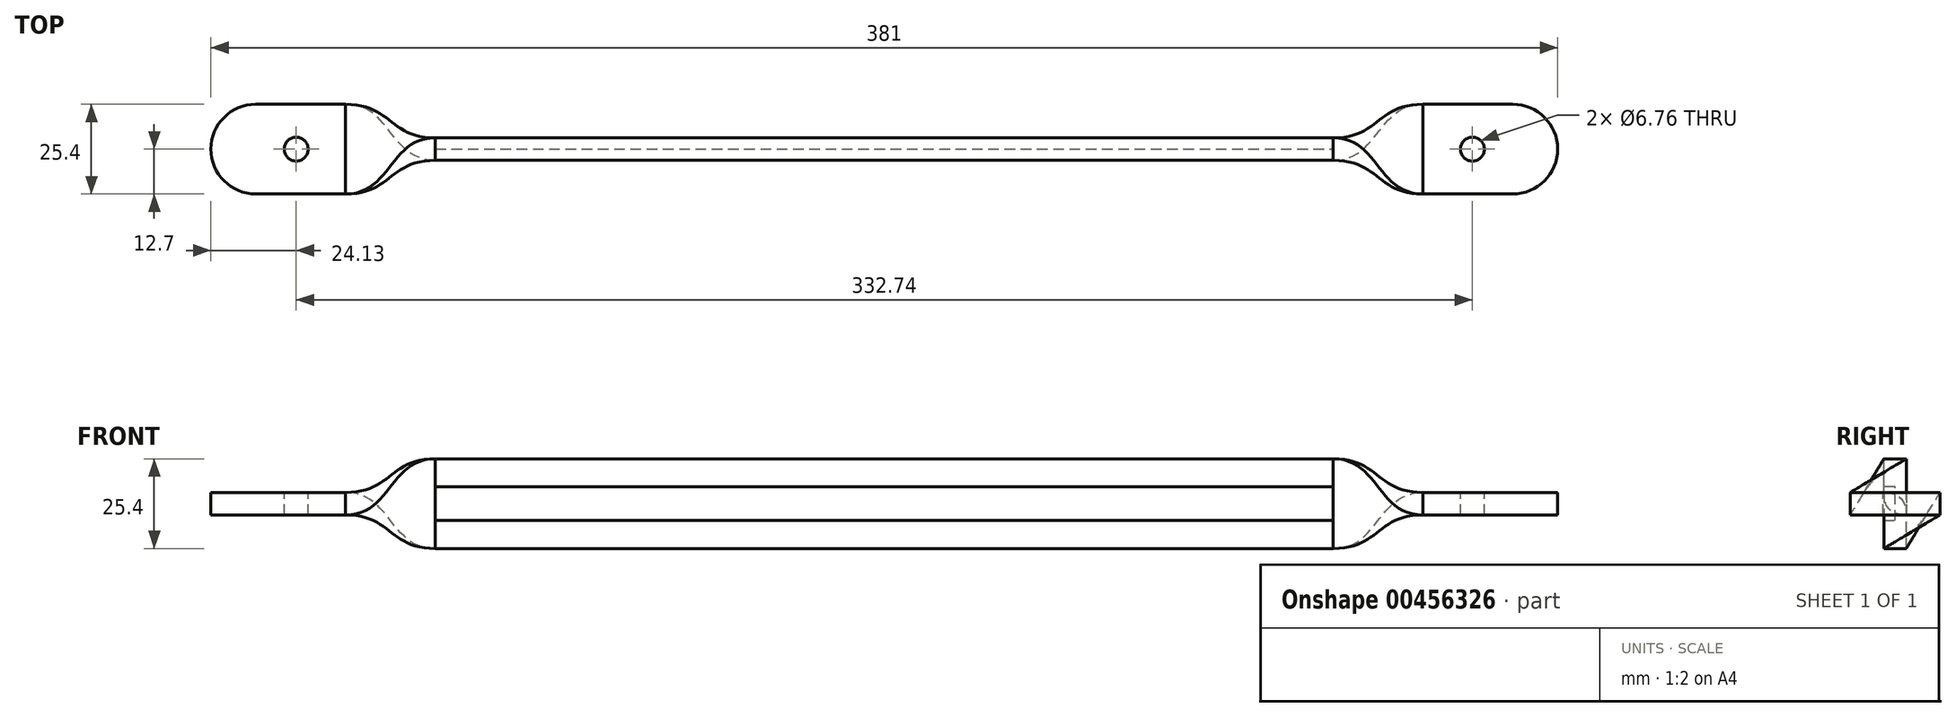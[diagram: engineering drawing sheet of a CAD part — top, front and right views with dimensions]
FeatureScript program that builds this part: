
annotation { "Feature Type Name" : "Feature", "Feature Type Description" : "" }
export const myFeature = defineFeature(function(context is Context, id is Id, definition is map)
    precondition{}
    {
        {
            var Q0;
            Q0=qCreatedBy(makeId("Top.planeOp"),FACE);
            var sketch = newSketch(context, id + "F0", { "sketchPlane" : qUnion([Q0])});
            skPoint(sketch, "E0", {"position": v(-152.4, 12.7) * mm});
            skPoint(sketch, "E1", {"position": v(-152.4, -12.7) * mm});
            skPoint(sketch, "E2", {"position": v(0, 0) * mm});
            skPoint(sketch, "E3", {"position": v(-190.5, 12.7) * mm});
            skPoint(sketch, "E4", {"position": v(-190.5, -12.7) * mm});
            skLineSegment(sketch, "E5", {"start": v(-190.5, 0) * mm, "end": v(190.5, 0) * mm, "construction": true});
            skLineSegment(sketch, "E6", {"start": v(-177.8, 12.7) * mm, "end": v(-152.4, 12.7) * mm});
            skLineSegment(sketch, "E7", {"start": v(-152.4, -12.7) * mm, "end": v(-152.4, 12.7) * mm});
            skLineSegment(sketch, "E8", {"start": v(-177.8, -12.7) * mm, "end": v(-152.4, -12.7) * mm});
            skLineSegment(sketch, "E9", {"start": v(-190.5, 0) * mm, "end": v(-190.5, 0) * mm});
            skLineSegment(sketch, "E10", {"start": v(0, 12.7) * mm, "end": v(0, -12.7) * mm, "construction": true});
            skPoint(sketch, "E11", {"position": v(-166.37, 0) * mm});
            skArc(sketch, "E12.filletArc", {"start": v(-190.5, 0) * mm, "mid": v(-186.78, -8.98) * mm, "end": v(-177.8, -12.7) * mm});
            skArc(sketch, "E13.filletArc", {"start": v(-177.8, 12.7) * mm, "mid": v(-186.78, 8.98) * mm, "end": v(-190.5, 0) * mm});
            skSolve(sketch);
        }
        {
            var Q0;
            Q0=makeQuery(id+"F0.imprint","IMPRINT",FACE,{"disambiguationData":[TD([[makeQuery(id+"F0.imprint","IMPRINT",EDGE,{"derivedFrom":sQuery(id+"F0.wireOp",EDGE,"33ddd2f7-314b-40ee-8d08-8bc8de4d81912.MirrorCS")}),1.0]])]});
            var Q1;
            Q1=makeQuery(id+"F0.imprint","IMPRINT",FACE,{"disambiguationData":[TD([[makeQuery(id+"F0.imprint","IMPRINT",EDGE,{"derivedFrom":sQuery(id+"F0.wireOp",EDGE,"E6")}),-1.0]])]});
            extrude(context, id + "F1", {"entities" : qUnion([Q0, Q1]), "endBound" : BoundingType.SYMMETRIC, "depth" : 6.35 * mm});
        }
        {
            var Q0;
            Q0=sQuery(id+"F0.wireOp",VERTEX,"E11");
            var Q1;
            Q1=makeQuery(id+"F1.opExtrude","SWEPT_BODY",BODY,{"disambiguationData":[OSD([sQuery(id+"F0.wireOp",EDGE,"E6"),sQuery(id+"F0.wireOp",EDGE,"E7"),sQuery(id+"F0.wireOp",EDGE,"E8"),sQuery(id+"F0.wireOp",EDGE,"E12.filletArc"),sQuery(id+"F0.wireOp",EDGE,"E13.filletArc")])]});
            hole(context, id + "F2", {"style" : HoleStyle.SIMPLE, "endStyle" : HoleEndStyle.THROUGH, "standardTappedOrClearance" : lookupTablePath({ "standard" : "ANSI", "fit" : "Normal (ASME)", "size" : "1/4", "type" : "Clearance" }), "standardBlindInLast" : lookupTablePath({ "fit" : "Free", "standard" : "ANSI", "size" : "1/4", "type" : "Clearance" }), "holeDiameter" : 6.76 * mm, "isTappedThrough" : true, "tappedDepth" : 12.7 * mm, "tapClearance" : 3, "locations" : qUnion([Q0]), "scope" : qUnion([Q1])});
        }
        {
            var Q0;
            Q0=sQuery(id+"F0.wireOp",VERTEX,"E11");
            var Q1;
            Q1=makeQuery(id+"F1.opExtrude","SWEPT_BODY",BODY,{"disambiguationData":[OSD([sQuery(id+"F0.wireOp",EDGE,"E6"),sQuery(id+"F0.wireOp",EDGE,"E7"),sQuery(id+"F0.wireOp",EDGE,"E8"),sQuery(id+"F0.wireOp",EDGE,"E12.filletArc"),sQuery(id+"F0.wireOp",EDGE,"E13.filletArc")])]});
            hole(context, id + "F3", {"style" : HoleStyle.SIMPLE, "endStyle" : HoleEndStyle.THROUGH, "oppositeDirection" : true, "standardTappedOrClearance" : lookupTablePath({ "standard" : "ANSI", "fit" : "Normal (ASME)", "size" : "1/4", "type" : "Clearance" }), "standardBlindInLast" : lookupTablePath({ "fit" : "Free", "standard" : "ANSI", "size" : "1/4", "type" : "Clearance" }), "holeDiameter" : 6.76 * mm, "isTappedThrough" : true, "tappedDepth" : 12.7 * mm, "tapClearance" : 3, "locations" : qUnion([Q0]), "scope" : qUnion([Q1])});
        }
        {
            var Q0;
            Q0=makeQuery(id+"F1.opExtrude","SWEPT_BODY",BODY,{"disambiguationData":[OSD([sQuery(id+"F0.wireOp",EDGE,"E6"),sQuery(id+"F0.wireOp",EDGE,"E7"),sQuery(id+"F0.wireOp",EDGE,"E8"),sQuery(id+"F0.wireOp",EDGE,"E12.filletArc"),sQuery(id+"F0.wireOp",EDGE,"E13.filletArc")])]});
            var Q1;
            Q1=qCreatedBy(makeId("Right.planeOp"),FACE);
            mirror(context, id + "F4", {"entities" : qUnion([Q0]), "mirrorPlane" : qUnion([Q1])});
        }
        {
            var Q0;
            Q0=qCreatedBy(makeId("Front.planeOp"),FACE);
            var sketch = newSketch(context, id + "F5", { "sketchPlane" : qUnion([Q0])});
            skPoint(sketch, "E14", {"position": v(0, 0) * mm});
            skLineSegment(sketch, "E15", {"start": v(-127, 0) * mm, "end": v(127, 0) * mm, "construction": true});
            skLineSegment(sketch, "E16", {"start": v(0, -12.7) * mm, "end": v(0, 12.7) * mm, "construction": true});
            skPoint(sketch, "E17", {"position": v(-127, -12.7) * mm});
            skPoint(sketch, "E18", {"position": v(-127, 12.7) * mm});
            skPoint(sketch, "E19", {"position": v(127, -12.7) * mm});
            skPoint(sketch, "E20", {"position": v(127, 12.7) * mm});
            skLineSegment(sketch, "E21", {"start": v(-127, -12.7) * mm, "end": v(-127, 12.7) * mm});
            skLineSegment(sketch, "E22", {"start": v(-127, 12.7) * mm, "end": v(127, 12.7) * mm});
            skLineSegment(sketch, "E23", {"start": v(127, 12.7) * mm, "end": v(127, -12.7) * mm});
            skLineSegment(sketch, "E24", {"start": v(127, -12.7) * mm, "end": v(-127, -12.7) * mm});
            skSolve(sketch);
        }
        {
            var Q0;
            Q0=makeQuery(id+"F5.imprint","IMPRINT",FACE,{"disambiguationData":[TD([[makeQuery(id+"F5.imprint","IMPRINT",EDGE,{"derivedFrom":sQuery(id+"F5.wireOp",EDGE,"E21")}),-1.0]])]});
            extrude(context, id + "F6", {"entities" : qUnion([Q0]), "endBound" : BoundingType.SYMMETRIC, "oppositeDirection" : true, "depth" : 6.35 * mm});
        }
        {
            var Q0;
            Q0=makeQuery(id+"F6.opExtrude","SWEPT_FACE",FACE,{"disambiguationData":[OSD([sQuery(id+"F5.wireOp",EDGE,"E21")])]});
            var Q1;
            Q1=makeQuery(id+"F1.opExtrude","SWEPT_FACE",FACE,{"disambiguationData":[OSD([sQuery(id+"F0.wireOp",EDGE,"E7")])]});
            var Q2;
            Q2=makeQuery(id+"F1.opExtrude","CAP_VERTEX",VERTEX,{"disambiguationData":[OSD([sQuery(id+"F0.wireOp",EDGE,"E6"),sQuery(id+"F0.wireOp",EDGE,"E7")])],"isStart":false});
            var Q3;
            Q3=makeQuery(id+"F6.opExtrude","CAP_VERTEX",VERTEX,{"disambiguationData":[OSD([sQuery(id+"F5.wireOp",EDGE,"E21"),sQuery(id+"F5.wireOp",EDGE,"E24")])],"isStart":false});
            loft(context, id + "F7", {"startCondition" : LoftEndDerivativeType.NORMAL_TO_PROFILE, "startMagnitude" : 1.5, "endCondition" : LoftEndDerivativeType.NORMAL_TO_PROFILE, "endMagnitude" : 1.5, "sheetProfilesArray" : [{ "sheetProfileEntities" : qUnion([Q0]) }, { "sheetProfileEntities" : qUnion([Q1]) }], "matchConnections" : true, "connections" : [{ "connectionEntities" : qUnion([Q2, Q3]), "connectionEdgeQueries" : qUnion([]), "connectionEdgeParameters" : [] }]});
        }
        {
            var Q0;
            Q0=makeQuery(id+"F6.opExtrude","SWEPT_FACE",FACE,{"disambiguationData":[OSD([sQuery(id+"F5.wireOp",EDGE,"E23")])]});
            var Q1;
            Q1=makeQuery(id+"F4.opPattern","COPY",FACE,{"derivedFrom":makeQuery(id+"F1.opExtrude","SWEPT_FACE",FACE,{"disambiguationData":[OSD([sQuery(id+"F0.wireOp",EDGE,"E7")])]}),"instanceName":"1"});
            var Q2;
            Q2=makeQuery(id+"F4.opPattern","COPY",VERTEX,{"derivedFrom":makeQuery(id+"F1.opExtrude","CAP_VERTEX",VERTEX,{"disambiguationData":[OSD([sQuery(id+"F0.wireOp",EDGE,"E6"),sQuery(id+"F0.wireOp",EDGE,"E7")])],"isStart":false}),"instanceName":"1"});
            var Q3;
            Q3=makeQuery(id+"F6.opExtrude","CAP_VERTEX",VERTEX,{"disambiguationData":[OSD([sQuery(id+"F5.wireOp",EDGE,"E23"),sQuery(id+"F5.wireOp",EDGE,"E24")])],"isStart":false});
            loft(context, id + "F8", {"startCondition" : LoftEndDerivativeType.NORMAL_TO_PROFILE, "startMagnitude" : 1.5, "endCondition" : LoftEndDerivativeType.NORMAL_TO_PROFILE, "endMagnitude" : 1.5, "sheetProfilesArray" : [{ "sheetProfileEntities" : qUnion([Q0]) }, { "sheetProfileEntities" : qUnion([Q1]) }], "matchConnections" : true, "connections" : [{ "connectionEntities" : qUnion([Q2, Q3]), "connectionEdgeQueries" : qUnion([]), "connectionEdgeParameters" : [] }]});
        }
        {
            var Q0;
            Q0=qCreatedBy(makeId("Right.planeOp"),FACE);
            var sketch = newSketch(context, id + "F9", { "sketchPlane" : qUnion([Q0])});
            skPoint(sketch, "E25", {"position": v(0, 0) * mm});
            skLineSegment(sketch, "E26", {"start": v(0, 4.76) * mm, "end": v(0, -4.76) * mm});
            skPoint(sketch, "E27", {"position": v(-3.18, -4.76) * mm});
            skPoint(sketch, "E28", {"position": v(-3.18, 4.76) * mm});
            skLineSegment(sketch, "E29", {"start": v(0, -4.76) * mm, "end": v(-3.18, -4.76) * mm});
            skLineSegment(sketch, "E30", {"start": v(-3.18, 4.76) * mm, "end": v(-3.18, -4.76) * mm});
            skLineSegment(sketch, "E31", {"start": v(-3.18, 4.76) * mm, "end": v(0, 4.76) * mm});
            skSolve(sketch);
        }
        {
            var Q0;
            Q0=qSketchRegion(id+"F9",true);
            var Q1;
            Q1=makeQuery(id+"F6.opExtrude","SWEPT_FACE",FACE,{"disambiguationData":[OSD([sQuery(id+"F5.wireOp",EDGE,"E21")])]});
            var Q2;
            Q2=makeQuery(id+"F6.opExtrude","SWEPT_FACE",FACE,{"disambiguationData":[OSD([sQuery(id+"F5.wireOp",EDGE,"E23")])]});
            extrude(context, id + "F10", {"entities" : qUnion([Q0]), "operationType" : NewBodyOperationType.REMOVE, "endBound" : BoundingType.UP_TO_SURFACE, "oppositeDirection" : true, "endBoundEntityFace" : qUnion([Q1]), "depth" : 25.4 * mm, "hasSecondDirection" : true, "secondDirectionBound" : SecondDirectionBoundingType.UP_TO_SURFACE, "secondDirectionOppositeDirection" : false, "secondDirectionBoundEntityFace" : qUnion([Q2]), "secondDirectionDepth" : 25.4 * mm});
        }
    });
